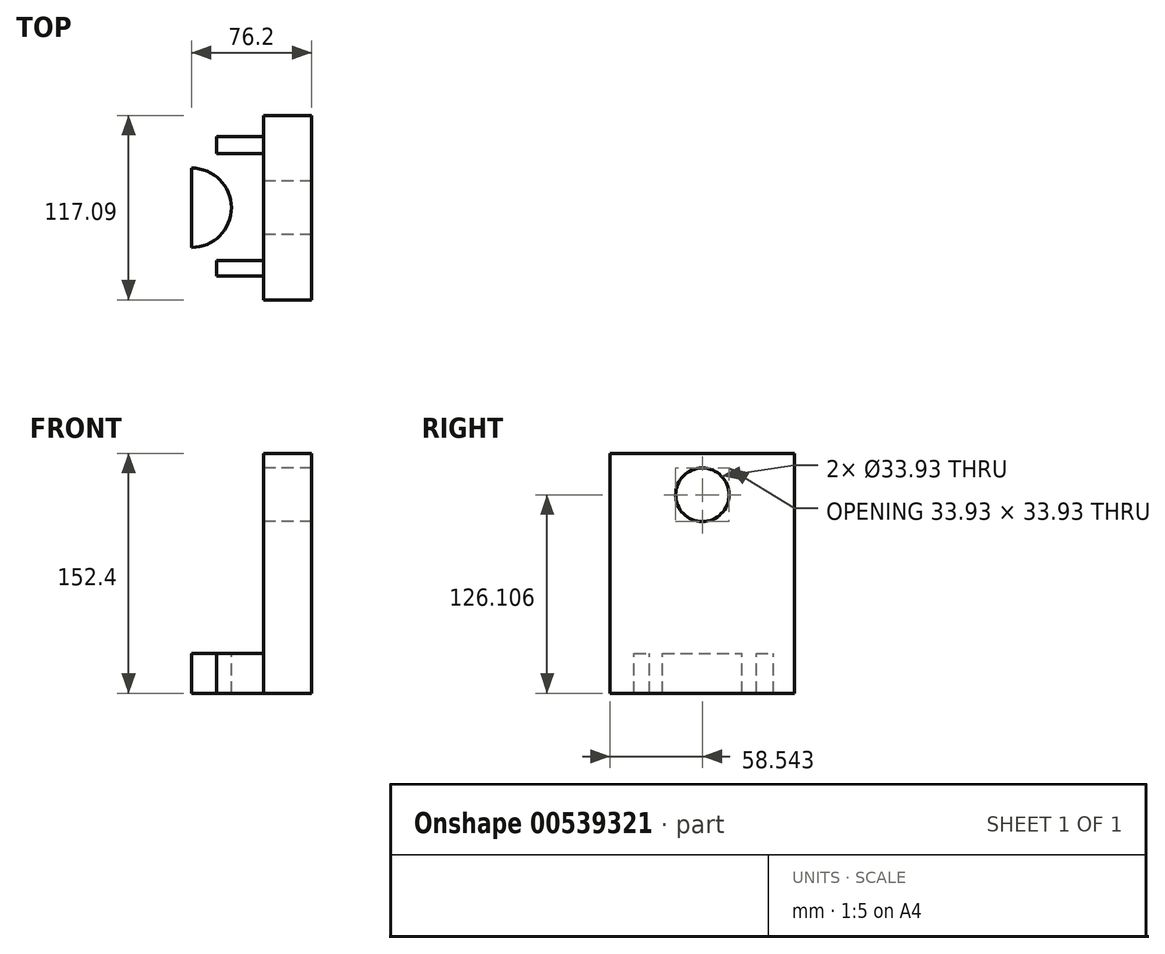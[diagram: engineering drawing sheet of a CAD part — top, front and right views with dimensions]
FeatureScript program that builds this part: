
annotation { "Feature Type Name" : "Feature", "Feature Type Description" : "" }
export const myFeature = defineFeature(function(context is Context, id is Id, definition is map)
    precondition{}
    {
        {
            var Q0;
            Q0=qCreatedBy(makeId("Front.planeOp"),FACE);
            var sketch = newSketch(context, id + "F0", { "sketchPlane" : qUnion([Q0])});
            skLineSegment(sketch, "E0", {"start": v(0, 0) * mm, "end": v(-76.2, 0) * mm});
            skLineSegment(sketch, "E1", {"start": v(-76.2, 0) * mm, "end": v(-76.2, 25.4) * mm});
            skLineSegment(sketch, "E2", {"start": v(-76.2, 25.4) * mm, "end": v(-30.48, 25.4) * mm});
            skLineSegment(sketch, "E3", {"start": v(-30.48, 25.4) * mm, "end": v(-30.48, 152.4) * mm});
            skLineSegment(sketch, "E4", {"start": v(-30.48, 152.4) * mm, "end": v(0, 152.4) * mm});
            skLineSegment(sketch, "E5", {"start": v(0, 152.4) * mm, "end": v(0, 0) * mm});
            skSolve(sketch);
        }
        {
            var Q0;
            Q0 = qSketchRegion(id + "F0", true);
            extrude(context, id + "F1", {"entities" : qUnion([Q0]), "depth" : 117.1 * mm, "offsetDistance" : 25.4 * mm});
        }
        {
            var Q0;
            Q0=makeQuery(id+"F1.opExtrude","SWEPT_FACE",FACE,{"disambiguationData":[OSD([sQuery(id+"F0.wireOp",EDGE,"E3")])]});
            var sketch = newSketch(context, id + "F2", { "sketchPlane" : qUnion([Q0])});
            skCircle(sketch, "E6", {"center": v(58.55, 126.1) * mm, "radius": 16.96 * mm});
            skPoint(sketch, "E6.centerSnap0", {"position": v(58.55, 152.4) * mm});
            skCircle(sketch, "E7", {"center": v(58.55, 126.1) * mm, "radius": 9.94 * mm});
            skSolve(sketch);
        }
        {
            var Q0;
            Q0=makeQuery(id+"F1.opExtrude","SWEPT_FACE",FACE,{"disambiguationData":[OSD([sQuery(id+"F0.wireOp",EDGE,"E2")])]});
            var sketch = newSketch(context, id + "F3", { "sketchPlane" : qUnion([Q0])});
            skLineSegment(sketch, "E8.bottom", {"start": v(-30.48, -13.49) * mm, "end": v(-60.37, -13.49) * mm});
            skLineSegment(sketch, "E8.top", {"start": v(-30.48, -24.24) * mm, "end": v(-60.37, -24.24) * mm});
            skLineSegment(sketch, "E8.left", {"start": v(-30.48, -13.49) * mm, "end": v(-30.48, -24.24) * mm});
            skLineSegment(sketch, "E8.right", {"start": v(-60.37, -13.49) * mm, "end": v(-60.37, -24.24) * mm});
            skLineSegment(sketch, "E9.bottom", {"start": v(-30.48, -92.03) * mm, "end": v(-60.37, -92.03) * mm});
            skLineSegment(sketch, "E9.top", {"start": v(-30.48, -101.95) * mm, "end": v(-60.37, -101.95) * mm});
            skLineSegment(sketch, "E9.left", {"start": v(-30.48, -92.03) * mm, "end": v(-30.48, -101.95) * mm});
            skLineSegment(sketch, "E9.right", {"start": v(-60.37, -92.03) * mm, "end": v(-60.37, -101.95) * mm});
            skArc(sketch, "E10", {"start": v(-76.2, -33.33) * mm, "mid": v(-50.98, -58.55) * mm, "end": v(-76.2, -83.76) * mm});
            skSolve(sketch);
        }
        {
            var Q0;
            {var subQ0=sQuery(id+"F3.wireOp",EDGE,"E10");Q0=makeQuery(id+"F3.imprint","IMPRINT",FACE,{"disambiguationData":[TD([[makeQuery(id+"F3.imprint","IMPRINT",EDGE,{"derivedFrom":subQ0}),-1.0]])]});}
            extrude(context, id + "F4", {"entities" : qUnion([Q0]), "operationType" : NewBodyOperationType.REMOVE, "oppositeDirection" : true, "depth" : 25.4 * mm, "offsetDistance" : 25.4 * mm});
        }
        {
            var Q0;
            Q0=makeQuery(id+"F2.imprint","IMPRINT",FACE,{"disambiguationData":[TD([[makeQuery(id+"F2.imprint","IMPRINT",EDGE,{"derivedFrom":sQuery(id+"F2.wireOp",EDGE,"E7")}),1.0]])]});
            var Q1;
            Q1=makeQuery(id+"F2.imprint","IMPRINT",FACE,{"disambiguationData":[TD([[makeQuery(id+"F2.imprint","IMPRINT",EDGE,{"derivedFrom":sQuery(id+"F2.wireOp",EDGE,"E6")}),1.0]])]});
            extrude(context, id + "F5", {"entities" : qUnion([Q0, Q1]), "operationType" : NewBodyOperationType.REMOVE, "oppositeDirection" : true, "depth" : 65.28 * mm, "offsetDistance" : 25.4 * mm});
        }
    });
